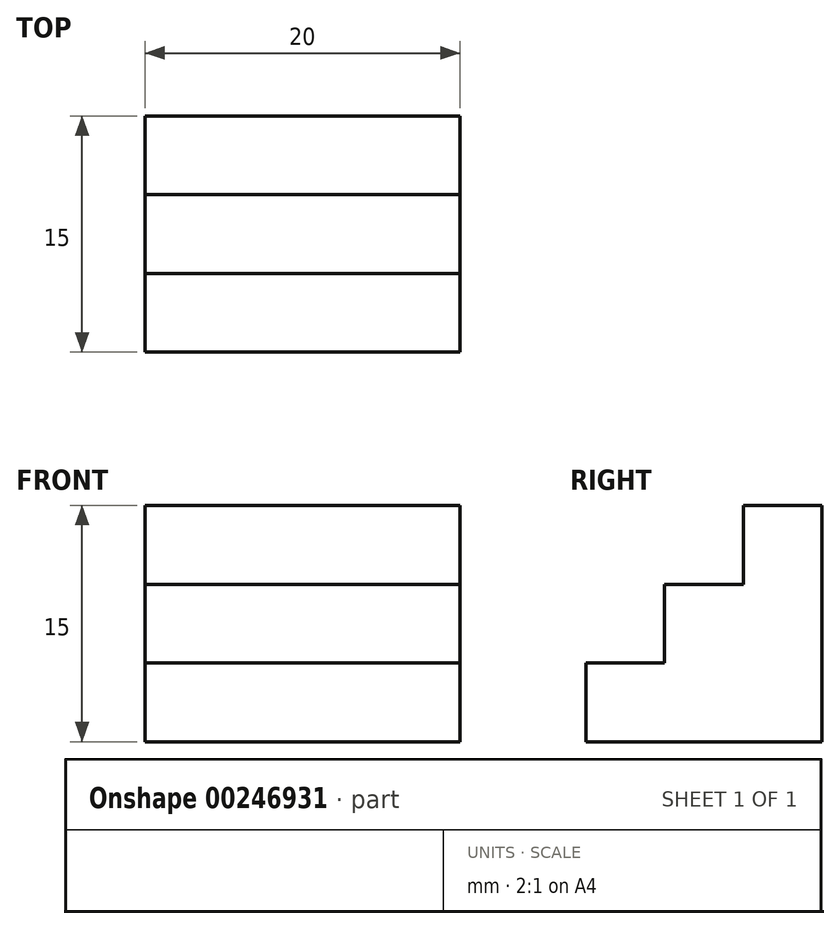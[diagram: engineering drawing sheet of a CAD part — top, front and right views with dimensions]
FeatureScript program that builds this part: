
annotation { "Feature Type Name" : "Feature", "Feature Type Description" : "" }
export const myFeature = defineFeature(function(context is Context, id is Id, definition is map)
    precondition{}
    {
        {
            var Q0;
            Q0=qCreatedBy(makeId("Front.planeOp"),FACE);
            var sketch = newSketch(context, id + "F0", { "sketchPlane" : qUnion([Q0])});
            skLineSegment(sketch, "E0", {"start": v(0, 0) * mm, "end": v(20, 0) * mm});
            skLineSegment(sketch, "E1", {"start": v(20, 0) * mm, "end": v(20, 15) * mm});
            skLineSegment(sketch, "E2", {"start": v(20, 15) * mm, "end": v(0, 15) * mm});
            skLineSegment(sketch, "E3", {"start": v(0, 15) * mm, "end": v(0, 10) * mm});
            skLineSegment(sketch, "E4", {"start": v(0, 10) * mm, "end": v(0, 5) * mm});
            skLineSegment(sketch, "E5", {"start": v(0, 5) * mm, "end": v(0, 0) * mm});
            skLineSegment(sketch, "E6", {"start": v(0, 10) * mm, "end": v(20, 10) * mm});
            skLineSegment(sketch, "E7", {"start": v(0, 5) * mm, "end": v(20, 5) * mm});
            skSolve(sketch);
        }
        {
            var Q0;
            {var subQ0=sQuery(id+"F0.wireOp",EDGE,"E0");Q0=makeQuery(id+"F0.imprint","IMPRINT",FACE,{"disambiguationData":[TD([[makeQuery(id+"F0.imprint","IMPRINT",EDGE,{"derivedFrom":subQ0}),1.0]])]});}
            extrude(context, id + "F1", {"entities" : qUnion([Q0]), "depth" : 15 * mm});
        }
        {
            var Q0;
            Q0=makeQuery(id+"F0.imprint","IMPRINT",FACE,{"disambiguationData":[TD([[makeQuery(id+"F0.imprint","IMPRINT",EDGE,{"derivedFrom":sQuery(id+"F0.wireOp",EDGE,"E4")}),1.0]])]});
            extrude(context, id + "F2", {"entities" : qUnion([Q0]), "operationType" : NewBodyOperationType.ADD, "depth" : 10 * mm});
        }
        {
            var Q0;
            {var subQ0=sQuery(id+"F0.wireOp",EDGE,"E2");Q0=makeQuery(id+"F0.imprint","IMPRINT",FACE,{"disambiguationData":[TD([[makeQuery(id+"F0.imprint","IMPRINT",EDGE,{"derivedFrom":subQ0}),1.0]])]});}
            extrude(context, id + "F3", {"entities" : qUnion([Q0]), "operationType" : NewBodyOperationType.ADD, "depth" : 5 * mm});
        }
    });
